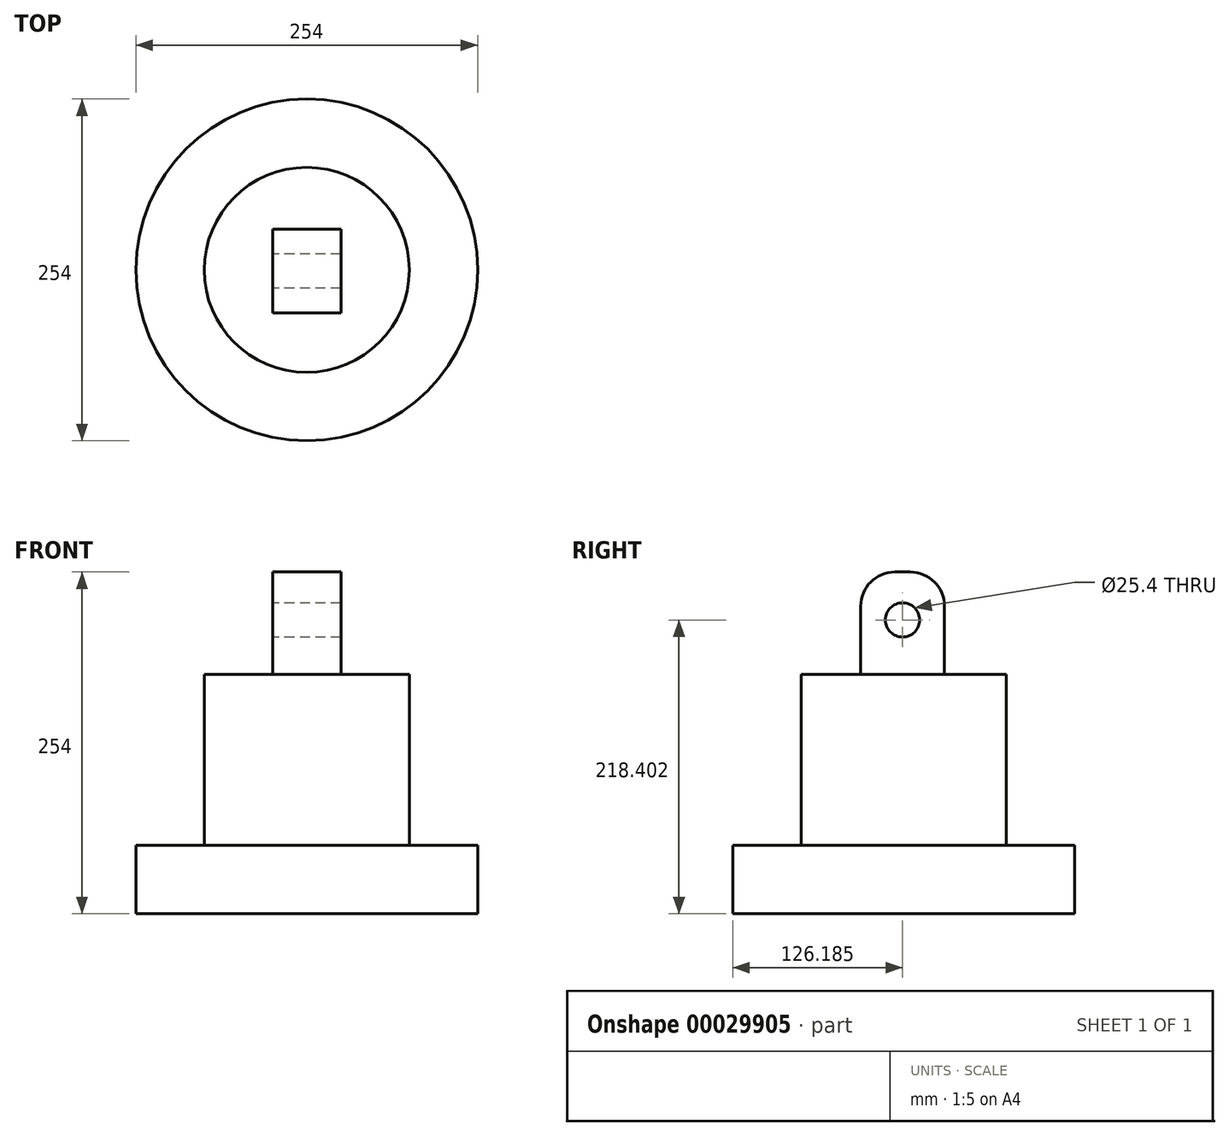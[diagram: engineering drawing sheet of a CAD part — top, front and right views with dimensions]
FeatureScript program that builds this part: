
annotation { "Feature Type Name" : "Feature", "Feature Type Description" : "" }
export const myFeature = defineFeature(function(context is Context, id is Id, definition is map)
    precondition{}
    {
        {
            var Q0;
            Q0=qCreatedBy(makeId("Front.planeOp"),FACE);
            var sketch = newSketch(context, id + "F0", { "sketchPlane" : qUnion([Q0])});
            skLineSegment(sketch, "E0", {"start": v(-155.87, 46) * mm, "end": v(-155.87, -4.8) * mm});
            skLineSegment(sketch, "E1", {"start": v(-155.87, -4.8) * mm, "end": v(-28.87, -4.8) * mm});
            skLineSegment(sketch, "E2", {"start": v(-28.87, -4.8) * mm, "end": v(-28.87, 46) * mm});
            skLineSegment(sketch, "E3", {"start": v(-28.87, 46) * mm, "end": v(-155.87, 46) * mm});
            skSolve(sketch);
        }
        {
            var Q0;
            Q0=makeQuery(id+"F0.imprint","IMPRINT",FACE,{"disambiguationData":[TD([[makeQuery(id+"F0.imprint","IMPRINT",EDGE,{"derivedFrom":sQuery(id+"F0.wireOp",EDGE,"E0")}),1.0]])]});
            var Q1;
            Q1=sQuery(id+"F0.wireOp",EDGE,"E0");
            revolve(context, id + "F1", {"entities" : qUnion([Q0]), "axis" : qUnion([Q1]), "revolveType" : RevolveType.FULL});
        }
        {
            var Q0;
            Q0=makeQuery(id+"F1.opRevolve","SWEPT_FACE",FACE,{"disambiguationData":[OSD([sQuery(id+"F0.wireOp",EDGE,"E3")])]});
            var sketch = newSketch(context, id + "F2", { "sketchPlane" : qUnion([Q0])});
            skCircle(sketch, "E4", {"center": v(-155.87, 0) * mm, "radius": 76.2 * mm});
            skSolve(sketch);
        }
        {
            var Q0;
            Q0=qSketchRegion(id+"F2",true);
            extrude(context, id + "F3", {"entities" : qUnion([Q0]), "operationType" : NewBodyOperationType.ADD, "depth" : 127 * mm});
        }
        {
            var Q0;
            Q0=makeQuery(id+"F3.opExtrude","CAP_FACE",FACE,{"disambiguationData":[OSD([sQuery(id+"F2.wireOp",EDGE,"E4")])],"isStart":false});
            var sketch = newSketch(context, id + "F4", { "sketchPlane" : qUnion([Q0])});
            skLineSegment(sketch, "E5", {"start": v(-155.87, 30.3) * mm, "end": v(-130.47, 30.3) * mm});
            skLineSegment(sketch, "E6", {"start": v(-130.47, 30.3) * mm, "end": v(-130.47, -31.94) * mm});
            skLineSegment(sketch, "E7", {"start": v(-130.47, -31.94) * mm, "end": v(-155.87, -31.94) * mm});
            skLineSegment(sketch, "E8", {"start": v(-155.87, 30.3) * mm, "end": v(-181.27, 30.3) * mm});
            skLineSegment(sketch, "E9", {"start": v(-181.27, 30.3) * mm, "end": v(-181.27, -31.94) * mm});
            skLineSegment(sketch, "E10", {"start": v(-181.27, -31.94) * mm, "end": v(-155.87, -31.94) * mm});
            skPoint(sketch, "E11.start.orphan", {"position": v(-155.87, 0) * mm});
            skSolve(sketch);
        }
        {
            var Q0;
            Q0=makeQuery(id+"F4.imprint","IMPRINT",FACE,{"disambiguationData":[TD([[makeQuery(id+"F4.imprint","IMPRINT",EDGE,{"derivedFrom":sQuery(id+"F4.wireOp",EDGE,"E5")}),-1.0]])]});
            extrude(context, id + "F5", {"entities" : qUnion([Q0]), "operationType" : NewBodyOperationType.ADD, "depth" : 76.2 * mm});
        }
        {
            var Q0;
            Q0=makeQuery(id+"F5.opExtrude","CAP_EDGE",EDGE,{"disambiguationData":[OSD([sQuery(id+"F4.wireOp",EDGE,"E5"),sQuery(id+"F4.wireOp",EDGE,"E8")])],"isStart":false});
            fillet(context, id + "F6", {"entities" : qUnion([Q0]), "radius" : 25.4 * mm, "tangentPropagation" : true, "allowEdgeOverflow" : false});
        }
        {
            var Q0;
            Q0=makeQuery(id+"F5.opExtrude","CAP_EDGE",EDGE,{"disambiguationData":[OSD([sQuery(id+"F4.wireOp",EDGE,"E7"),sQuery(id+"F4.wireOp",EDGE,"E10")])],"isStart":false});
            fillet(context, id + "F7", {"entities" : qUnion([Q0]), "radius" : 25.4 * mm, "tangentPropagation" : true, "allowEdgeOverflow" : false});
        }
        {
            var Q0;
            Q0=makeQuery(id+"F5.opExtrude","SWEPT_FACE",FACE,{"disambiguationData":[OSD([sQuery(id+"F4.wireOp",EDGE,"E9")])]});
            var sketch = newSketch(context, id + "F8", { "sketchPlane" : qUnion([Q0])});
            skCircle(sketch, "E12", {"center": v(0.81, 213.61) * mm, "radius": 12.7 * mm});
            skSolve(sketch);
        }
        {
            var Q0;
            Q0=makeQuery(id+"F8.imprint","IMPRINT",FACE,{"disambiguationData":[TD([[makeQuery(id+"F8.imprint","IMPRINT",EDGE,{"derivedFrom":sQuery(id+"F8.wireOp",EDGE,"E12")}),1.0]])]});
            extrude(context, id + "F9", {"entities" : qUnion([Q0]), "operationType" : NewBodyOperationType.REMOVE, "endBound" : BoundingType.THROUGH_ALL, "oppositeDirection" : true, "depth" : 25.4 * mm});
        }
    });
